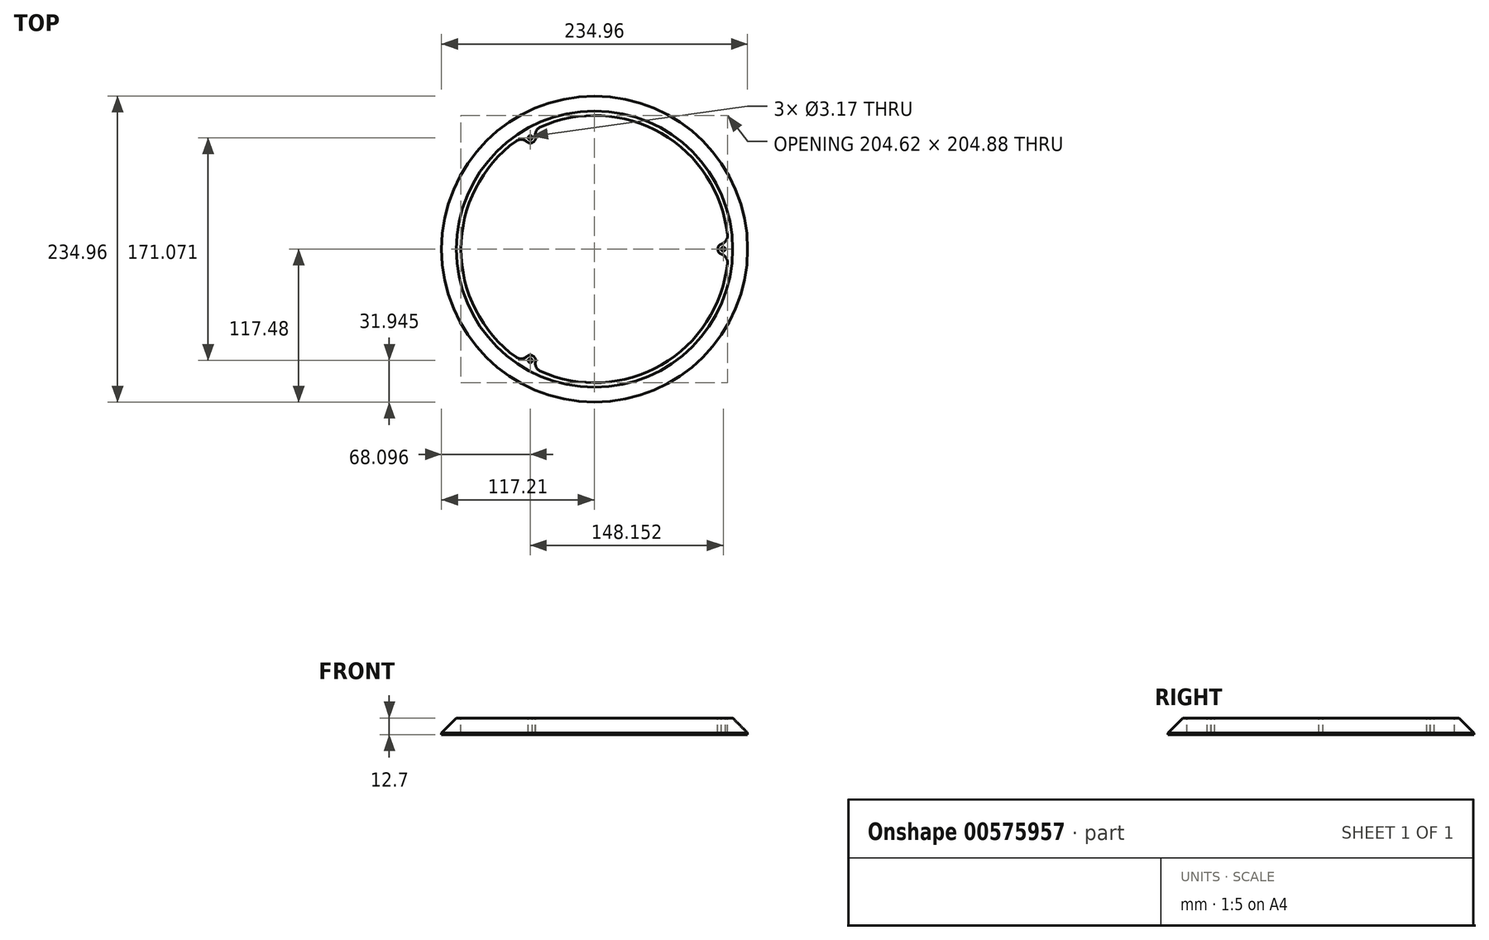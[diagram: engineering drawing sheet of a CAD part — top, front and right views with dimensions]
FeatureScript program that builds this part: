
annotation { "Feature Type Name" : "Feature", "Feature Type Description" : "" }
export const myFeature = defineFeature(function(context is Context, id is Id, definition is map)
    precondition{}
    {
        {
            var Q0;
            Q0=qCreatedBy(makeId("Top.planeOp"),FACE);
            var sketch = newSketch(context, id + "F0", { "sketchPlane" : qUnion([Q0])});
            skCircle(sketch, "E0", {"center": v(0, 0) * mm, "radius": 117.48 * mm});
            skCircle(sketch, "E1", {"center": v(0, 0) * mm, "radius": 94.62 * mm});
            skSolve(sketch);
        }
        {
            var Q0;
            Q0=makeQuery(id+"F0.imprint","IMPRINT",FACE,{"disambiguationData":[TD([[makeQuery(id+"F0.imprint","IMPRINT",EDGE,{"derivedFrom":sQuery(id+"F0.wireOp",EDGE,"E0")}),1.0]])]});
            extrude(context, id + "F1", {"entities" : qUnion([Q0]), "depth" : 12.7 * mm, "offsetDistance" : 25.4 * mm});
        }
        {
            var Q0;
            Q0=makeQuery(id+"F1.opExtrude","CAP_EDGE",EDGE,{"disambiguationData":[OSD([sQuery(id+"F0.wireOp",EDGE,"E0")])],"isStart":false});
            chamfer(context, id + "F2", {"entities" : qUnion([Q0]), "chamferType" : ChamferType.OFFSET_ANGLE, "width" : 11.43 * mm, "oppositeDirection" : false, "angle" : 45 * degree, "tangentPropagation" : true});
        }
        {
            var Q0;
            Q0=makeQuery(id+"F1.opExtrude","CAP_FACE",FACE,{"disambiguationData":[OSD([sQuery(id+"F0.wireOp",EDGE,"E0"),sQuery(id+"F0.wireOp",EDGE,"E1")])],"isStart":false});
            var sketch = newSketch(context, id + "F3", { "sketchPlane" : qUnion([Q0])});
            skArc(sketch, "E2", {"start": v(102.5, 4.15) * mm, "mid": v(51.3, 88.83) * mm, "end": v(-47.65, 90.84) * mm});
            skCircle(sketch, "E3", {"center": v(98.77, 0) * mm, "radius": 1.59 * mm});
            skArc(sketch, "E4", {"start": v(98.92, 4.15) * mm, "mid": v(94.62, 0.08) * mm, "end": v(98.77, -4.15) * mm});
            skLineSegment(sketch, "E5", {"start": v(98.92, 4.15) * mm, "end": v(102.5, 4.15) * mm});
            skLineSegment(sketch, "E6", {"start": v(98.77, -4.15) * mm, "end": v(102.5, -4.15) * mm});
            skArc(sketch, "E7.1.0", {"start": v(-53.05, 83.6) * mm, "mid": v(-47.37, 81.9) * mm, "end": v(-45.79, 87.61) * mm});
            skLineSegment(sketch, "E7.1.1", {"start": v(-45.79, 87.61) * mm, "end": v(-47.65, 90.84) * mm});
            skCircle(sketch, "E7.1.2", {"center": v(-49.38, 85.54) * mm, "radius": 1.59 * mm});
            skLineSegment(sketch, "E7.1.3", {"start": v(-53.05, 83.6) * mm, "end": v(-54.84, 86.69) * mm});
            skArc(sketch, "E7.2.0", {"start": v(-45.87, -87.74) * mm, "mid": v(-47.24, -81.98) * mm, "end": v(-52.98, -83.46) * mm});
            skLineSegment(sketch, "E7.2.1", {"start": v(-52.98, -83.46) * mm, "end": v(-54.84, -86.69) * mm});
            skCircle(sketch, "E7.2.2", {"center": v(-49.38, -85.54) * mm, "radius": 1.59 * mm});
            skLineSegment(sketch, "E7.2.3", {"start": v(-45.87, -87.74) * mm, "end": v(-47.65, -90.84) * mm});
            skArc(sketch, "E8.trimOffspring", {"start": v(-47.65, -90.84) * mm, "mid": v(51.29, -88.84) * mm, "end": v(102.5, -4.15) * mm});
            skArc(sketch, "E9.trimOffspring", {"start": v(-54.84, 86.69) * mm, "mid": v(-102.58, 0) * mm, "end": v(-54.84, -86.69) * mm});
            skSolve(sketch);
        }
        {
            var Q0;
            Q0=makeQuery(id+"F3.imprint","IMPRINT",FACE,{"disambiguationData":[TD([[makeQuery(id+"F3.imprint","IMPRINT",EDGE,{"derivedFrom":sQuery(id+"F3.wireOp",EDGE,"E7.2.2")}),1.0]])]});
            var Q1;
            Q1=makeQuery(id+"F3.imprint","IMPRINT",FACE,{"disambiguationData":[TD([[makeQuery(id+"F3.imprint","IMPRINT",EDGE,{"derivedFrom":sQuery(id+"F3.wireOp",EDGE,"E3")}),1.0]])]});
            var Q2;
            Q2=makeQuery(id+"F3.imprint","IMPRINT",FACE,{"disambiguationData":[TD([[makeQuery(id+"F3.imprint","IMPRINT",EDGE,{"derivedFrom":sQuery(id+"F3.wireOp",EDGE,"E7.1.2")}),1.0]])]});
            extrude(context, id + "F4", {"entities" : qUnion([Q0, Q1, Q2]), "operationType" : NewBodyOperationType.REMOVE, "oppositeDirection" : true, "depth" : 25.4 * mm, "offsetDistance" : 25.4 * mm});
        }
        {
            var Q0;
            {var subQ4=sQuery(id+"F3.wireOp",EDGE,"E7.1.3");Q0=makeQuery(id+"F3.imprint","IMPRINT",FACE,{"disambiguationData":[TD([[makeQuery(id+"F3.imprint","IMPRINT",EDGE,{"derivedFrom":subQ4}),1.0]])]});}
            var Q1;
            Q1=makeQuery(id+"F3.imprint","IMPRINT",FACE,{"disambiguationData":[TD([[makeQuery(id+"F3.imprint","IMPRINT",EDGE,{"derivedFrom":sQuery(id+"F3.wireOp",EDGE,"E2")}),1.0]])]});
            var Q2;
            {var subQ4=sQuery(id+"F3.wireOp",EDGE,"E6");Q2=makeQuery(id+"F3.imprint","IMPRINT",FACE,{"disambiguationData":[TD([[makeQuery(id+"F3.imprint","IMPRINT",EDGE,{"derivedFrom":subQ4}),-1.0]])]});}
            extrude(context, id + "F5", {"entities" : qUnion([Q0, Q1, Q2]), "operationType" : NewBodyOperationType.REMOVE, "oppositeDirection" : true, "depth" : 25.4 * mm, "offsetDistance" : 25.4 * mm});
        }
        {
            var Q0;
            Q0=makeQuery(id+"F5.boolean.opBoolean","COPY",EDGE,{"derivedFrom":makeQuery(id+"F5.opExtrude","SWEPT_EDGE",EDGE,{"disambiguationData":[OSD([sQuery(id+"F3.wireOp",EDGE,"E7.1.3"),sQuery(id+"F3.wireOp",EDGE,"E9.trimOffspring")])]})});
            var Q1;
            Q1=makeQuery(id+"F5.boolean.opBoolean","COPY",EDGE,{"derivedFrom":makeQuery(id+"F5.opExtrude","SWEPT_EDGE",EDGE,{"disambiguationData":[OSD([sQuery(id+"F3.wireOp",EDGE,"E2"),sQuery(id+"F3.wireOp",EDGE,"E7.1.1")])]})});
            var Q2;
            Q2=makeQuery(id+"F5.boolean.opBoolean","COPY",EDGE,{"derivedFrom":makeQuery(id+"F5.opExtrude","SWEPT_EDGE",EDGE,{"disambiguationData":[OSD([sQuery(id+"F3.wireOp",EDGE,"E6"),sQuery(id+"F3.wireOp",EDGE,"E8.trimOffspring")])]})});
            var Q3;
            Q3=makeQuery(id+"F5.boolean.opBoolean","COPY",EDGE,{"derivedFrom":makeQuery(id+"F5.opExtrude","SWEPT_EDGE",EDGE,{"disambiguationData":[OSD([sQuery(id+"F3.wireOp",EDGE,"E2"),sQuery(id+"F3.wireOp",EDGE,"E5")])]})});
            var Q4;
            Q4=makeQuery(id+"F5.boolean.opBoolean","COPY",EDGE,{"derivedFrom":makeQuery(id+"F5.opExtrude","SWEPT_EDGE",EDGE,{"disambiguationData":[OSD([sQuery(id+"F3.wireOp",EDGE,"E7.2.1"),sQuery(id+"F3.wireOp",EDGE,"E9.trimOffspring")])]})});
            var Q5;
            Q5=makeQuery(id+"F5.boolean.opBoolean","COPY",EDGE,{"derivedFrom":makeQuery(id+"F5.opExtrude","SWEPT_EDGE",EDGE,{"disambiguationData":[OSD([sQuery(id+"F3.wireOp",EDGE,"E7.2.3"),sQuery(id+"F3.wireOp",EDGE,"E8.trimOffspring")])]})});
            fillet(context, id + "F6", {"entities" : qUnion([Q0, Q1, Q2, Q3, Q4, Q5]), "radius" : 6.35 * mm, "tangentPropagation" : true, "allowEdgeOverflow" : false});
        }
    });
